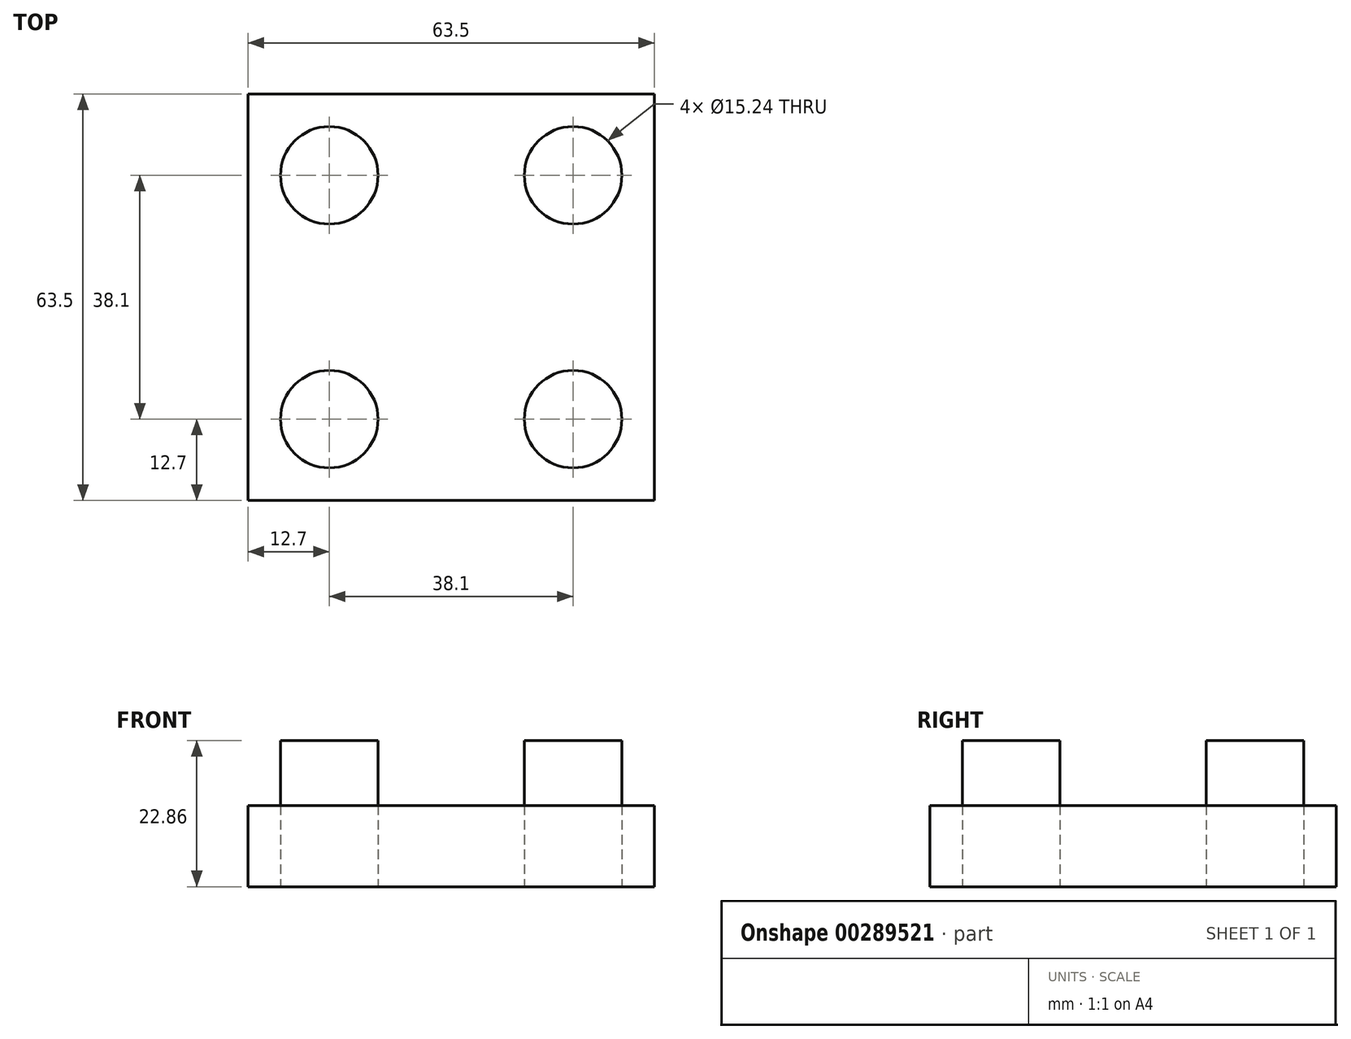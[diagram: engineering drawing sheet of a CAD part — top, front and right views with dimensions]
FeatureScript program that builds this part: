
annotation { "Feature Type Name" : "Feature", "Feature Type Description" : "" }
export const myFeature = defineFeature(function(context is Context, id is Id, definition is map)
    precondition{}
    {
        {
            var Q0;
            Q0=qCreatedBy(makeId("Top.planeOp"),FACE);
            var sketch = newSketch(context, id + "F0", { "sketchPlane" : qUnion([Q0])});
            skLineSegment(sketch, "E0.bottom", {"start": v(0, 0) * mm, "end": v(63.5, 0) * mm});
            skLineSegment(sketch, "E0.top", {"start": v(0, 63.5) * mm, "end": v(63.5, 63.5) * mm});
            skLineSegment(sketch, "E0.left", {"start": v(0, 0) * mm, "end": v(0, 63.5) * mm});
            skLineSegment(sketch, "E0.right", {"start": v(63.5, 0) * mm, "end": v(63.5, 63.5) * mm});
            skCircle(sketch, "E1", {"center": v(12.7, 50.8) * mm, "radius": 7.62 * mm});
            skCircle(sketch, "E2", {"center": v(12.7, 12.7) * mm, "radius": 7.62 * mm});
            skCircle(sketch, "E3", {"center": v(50.8, 12.7) * mm, "radius": 7.62 * mm});
            skCircle(sketch, "E4", {"center": v(50.8, 50.8) * mm, "radius": 7.62 * mm});
            skSolve(sketch);
        }
        {
            var Q0;
            Q0 = qSketchRegion(id + "F0", true);
            extrude(context, id + "F1", {"entities" : qUnion([Q0]), "depth" : 12.7 * mm});
        }
        {
            var Q0;
            Q0=makeQuery(id+"F1.opExtrude","CAP_FACE",FACE,{"disambiguationData":[OSD([sQuery(id+"F0.wireOp",EDGE,"E0.bottom"),sQuery(id+"F0.wireOp",EDGE,"E0.top"),sQuery(id+"F0.wireOp",EDGE,"E0.left"),sQuery(id+"F0.wireOp",EDGE,"E0.right"),sQuery(id+"F0.wireOp",EDGE,"E1"),sQuery(id+"F0.wireOp",EDGE,"E2"),sQuery(id+"F0.wireOp",EDGE,"E3"),sQuery(id+"F0.wireOp",EDGE,"E4")])],"isStart":false});
            var sketch = newSketch(context, id + "F2", { "sketchPlane" : qUnion([Q0])});
            skCircle(sketch, "E5", {"center": v(12.7, 50.8) * mm, "radius": 7.62 * mm});
            skCircle(sketch, "E6", {"center": v(12.7, 12.7) * mm, "radius": 7.62 * mm});
            skCircle(sketch, "E7", {"center": v(50.8, 12.7) * mm, "radius": 7.62 * mm});
            skCircle(sketch, "E8", {"center": v(50.8, 50.8) * mm, "radius": 7.62 * mm});
            skSolve(sketch);
        }
        {
            var Q0;
            Q0 = qSketchRegion(id + "F2", true);
            extrude(context, id + "F3", {"entities" : qUnion([Q0]), "depth" : 10.16 * mm});
        }
    });
